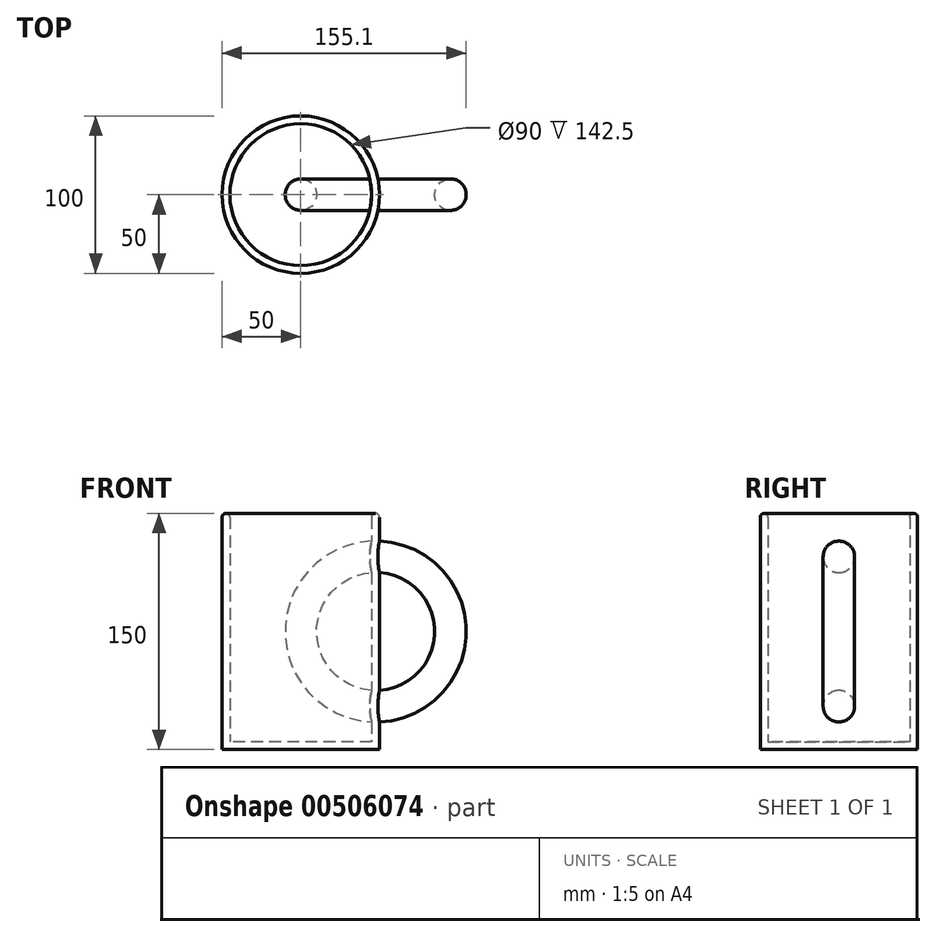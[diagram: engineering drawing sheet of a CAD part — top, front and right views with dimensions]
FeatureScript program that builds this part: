
annotation { "Feature Type Name" : "Feature", "Feature Type Description" : "" }
export const myFeature = defineFeature(function(context is Context, id is Id, definition is map)
    precondition{}
    {
        {
            var Q0;
            Q0=qCreatedBy(makeId("Top.planeOp"),FACE);
            var sketch = newSketch(context, id + "F0", { "sketchPlane" : qUnion([Q0])});
            skCircle(sketch, "E0", {"center": v(0, 0) * mm, "radius": 50 * mm});
            skSolve(sketch);
        }
        {
            var Q0;
            Q0 = qSketchRegion(id + "F0", true);
            extrude(context, id + "F1", {"entities" : qUnion([Q0]), "depth" : 150 * mm});
        }
        {
            var Q0;
            Q0=makeQuery(id+"F1.opExtrude","CAP_FACE",FACE,{"disambiguationData":[OSD([sQuery(id+"F0.wireOp",EDGE,"E0")])],"isStart":false});
            shell(context, id + "F2", {"entities" : qUnion([Q0]), "thickness" : 5 * mm});
        }
        {
            var Q0;
            Q0=makeQuery(id+"F1.opExtrude","CAP_EDGE",EDGE,{"disambiguationData":[OSD([sQuery(id+"F0.wireOp",EDGE,"E0")])],"isStart":false});
            var Q1;
            {var subQ0=sQuery(id+"F0.wireOp",EDGE,"E0");Q1=makeQuery(id+"F2.opShell","OFFSET_EDGE",EDGE,{"disambiguationData":[OSD([subQ0]),TDD([makeQuery(id+"F1.opExtrude","CAP_EDGE",EDGE,{"disambiguationData":[OSD([subQ0])],"isStart":false})])]});}
            fillet(context, id + "F3", {"entities" : qUnion([Q0, Q1]), "radius" : 2.5 * mm, "tangentPropagation" : true, "allowEdgeOverflow" : false});
        }
        {
            var Q0;
            Q0=qCreatedBy(makeId("Right.planeOp"),FACE);
            cPlane(context, id + "F4", {"entities" : qUnion([Q0]), "cplaneType" : CPlaneType.OFFSET, "offset" : 47.6 * mm, "width" : 150 * mm, "height" : 150 * mm});
        }
        {
            var Q0;
            Q0=qCreatedBy(id+"F4.planeOp",FACE);
            var sketch = newSketch(context, id + "F5", { "sketchPlane" : qUnion([Q0])});
            skCircle(sketch, "E1", {"center": v(0, 122.5) * mm, "radius": 10 * mm});
            skLineSegment(sketch, "E2", {"start": v(0, 75) * mm, "end": v(38.04, 75) * mm});
            skSolve(sketch);
        }
        {
            var Q0;
            Q0 = qSketchRegion(id + "F5", true);
            var Q1;
            Q1=sQuery(id+"F5.wireOp",EDGE,"E2");
            revolve(context, id + "F6", {"operationType" : NewBodyOperationType.ADD, "entities" : qUnion([Q0]), "axis" : qUnion([Q1]), "revolveType" : RevolveType.FULL});
        }
    });
